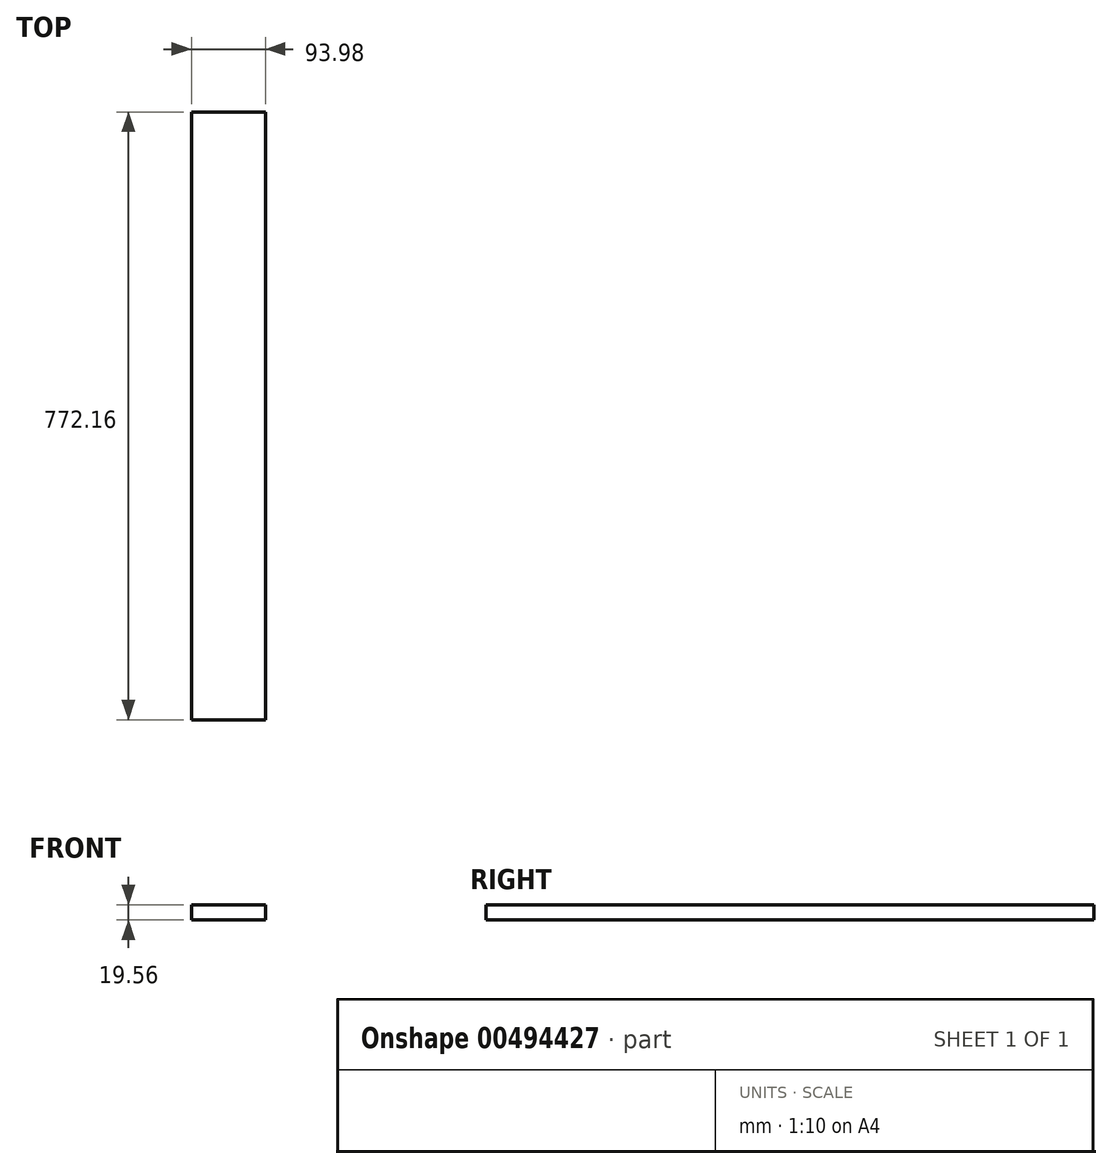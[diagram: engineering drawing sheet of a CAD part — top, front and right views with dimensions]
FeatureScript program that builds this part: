
annotation { "Feature Type Name" : "Feature", "Feature Type Description" : "" }
export const myFeature = defineFeature(function(context is Context, id is Id, definition is map)
    precondition{}
    {
        {
            var Q0;
            Q0=qCreatedBy(makeId("Front.planeOp"),FACE);
            var sketch = newSketch(context, id + "F0", { "sketchPlane" : qUnion([Q0])});
            skLineSegment(sketch, "E0.bottom", {"start": v(0, 0) * mm, "end": v(93.98, 0) * mm});
            skLineSegment(sketch, "E0.top", {"start": v(0, 19.56) * mm, "end": v(93.98, 19.56) * mm});
            skLineSegment(sketch, "E0.left", {"start": v(0, 0) * mm, "end": v(0, 19.56) * mm});
            skLineSegment(sketch, "E0.right", {"start": v(93.98, 0) * mm, "end": v(93.98, 19.56) * mm});
            skSolve(sketch);
        }
        {
            var Q0;
            Q0 = qSketchRegion(id + "F0", true);
            extrude(context, id + "F1", {"entities" : qUnion([Q0]), "depth" : 772.16 * mm});
        }
    });
